MODEL slx_dfd39811daf8
CONFIG AbsTol = auto
CONFIG EnableMultiTasking = off
CONFIG FixedStep = auto
CONFIG InitFcn = Wn = 10;
T = 0.001;
CONFIG MaxStep = auto
CONFIG MinStep = auto
CONFIG RelTol = 1e-3
CONFIG SampleTimeConstraint = Unconstrained
CONFIG SolverName = VariableStepAuto
CONFIG StartTime = 0.0
CONFIG StopTime = 5
BLOCK [CCaller] C Caller
  FunctionName = BPF_Loop
  PortSpecificationStruct = %)30     .    X ,   8    (     @         %    "     (    !     0         %  0 "0    $    _    07)G3F%M90  4&]R=$YA;64 4V-O<&4     26YD97@     5'EP90      4VEZ90      27-';&]B86P   X    X    !@    @    $          4    (     0    4    !         !     %    :6YP=70    .    .     8    (    !          %    "     $    %     0         0    !0   &EN<'5T    #@   #@    &    "     0         !0    @    !    !0...<+936ch>
BLOCK [Constant] Constant2
BLOCK [DataTypeConversion] Data Type Conversion
  RndMeth = Floor
  SaturateOnIntegerOverflow = off
BLOCK [DiscreteTransferFcn] Discrete Transfer Fcn8
  CloseFcn = dspblkCoreblockFVToolHelper(gcbh,'close');
  CopyFcn = dspblkCoreblockFVToolHelper(gcbh,'copy');
  DeleteFcn = dspblkCoreblockFVToolHelper(gcbh,'close');
  Denominator = [(8+8*T*Wn+4*T^2*Wn^2+T^3*Wn^3) (-24-8*T*Wn+4*T^2*Wn^2+3*T^3*Wn^3) (24-8*T*Wn-4*T^2*Wn^2+3*T^3*Wn^3) -8+8*T*Wn-4*T^2*Wn^2+T^3*Wn^3]
  InputPortMap = u0
  LoadFcn = dspblkCoreblockFVToolHelper(gcbh,'load');
  ModelCloseFcn = dspblkCoreblockFVToolHelper(gcbh,'close');
  Numerator = [(T^3*Wn^3) (3*T^3*Wn^3) (3*T^3*Wn^3) T^3*Wn^3]
  PostSaveFcn = dspblkCoreblockFVToolHelper(gcbh,'postsave');
  PreSaveFcn = dspblkCoreblockFVToolHelper(gcbh,'presave');
BLOCK [From] From7
  GotoTag = Signal
BLOCK [From] From9
  GotoTag = Signal
BLOCK [Goto] Goto
  GotoTag = Signal
BLOCK [Scope] Scope5
  ActiveDisplayYMaximum = 1.2063430691042178
  ActiveDisplayYMinimum = -0.13403798128244301
  DataLoggingVariableName = ScopeData5
  Floating = off
  GraphicalSettings = {"Style":{"BackgroundColor":[0.12941176470588237,0.12941176470588237,0.12941176470588237],"AxesColor":[0.07058823529411765,0.07058823529411765,0.07058823529411765],"LabelsColor":[0.8509803921568627,0.8509803921568627,0.8509803921568627],"PreserveColors":false,"Visible":[true,true],"LineStyle":["-","-"],"LineWidth":[1.5,1.5],"BarWidth":[0.9,0.9],"LineColor":["auto","auto"],"LineFaceAlpha":[1,1],"Li...<+2146ch>
  MultipleDisplayCache = [{"MaxYLimMag":1.2063430691042178,"MaxYLimReal":1.2063430691042178,"MinYLimMag":0,"MinYLimReal":-0.13403798128244301,"PlotAsMagnitudePhase":false,"ShowGrid":true,"ShowLegend":true,"Title":"%<SignalLabel>","YLabel":""}]
  NumInputPorts = 2
  ScopeFrameLocation = window
  ShowLegend = on
  WasSavedAsWebScope = on
  WindowPosition = [700.000000,308.000000,560.000000,420.000000,]
BLOCK [Sin] Sine Wave
  Amplitude = 200
  SampleTime = 0
BLOCK [Sin] Sine Wave1
  Amplitude = 8
  Frequency = 50
  SampleTime = 0
BLOCK [Sin] Sine Wave2
  Amplitude = 6
  Frequency = 500
  SampleTime = 0
BLOCK [Sin] Sine Wave3
  Amplitude = 2
  Frequency = 2000
  SampleTime = 0
BLOCK [Sin] Sine Wave4
  Amplitude = 20
  Frequency = 24
  SampleTime = 0
BLOCK [ZeroOrderHold] Zero-Order Hold6
  SampleTime = 0.001
BLOCK [TransferFcn] 一阶低通滤波
  Denominator = [1 Wn]
  Numerator = [Wn]
BLOCK [TransferFcn] 三阶低通滤波
  Denominator = [1 2*Wn 2*Wn^2 Wn^3]
  Numerator = [Wn^3]
BLOCK [TransferFcn] 二阶低通滤波
  Denominator = [1 sqrt(2)*Wn Wn^2]
  Numerator = [Wn^2]
BLOCK [Sum] 原始信号(1rad//s,带多个高频噪声)
  IconShape = rectangular
  Inputs = +++++
BLOCK [Scope] 示波器
  ActiveDisplayYMaximum = 289.66750049431852
  ActiveDisplayYMinimum = -289.523268507868
  DataLoggingVariableName = ScopeData6
  Floating = off
  GraphicalSettings = {"Style":{"BackgroundColor":[0.9019607843137255,0.9019607843137255,0.9019607843137255],"AxesColor":[0.9411764705882353,0.9411764705882353,0.9411764705882353],"LabelsColor":[0.5019607843137255,0.5019607843137255,0.5019607843137255],"PreserveColors":false,"Visible":[true,true,true,true],"LineStyle":["-","-","-","-"],"LineWidth":[1.5,1.5,1.5,1.5],"BarWidth":[0.9,0.9,0.9,0.9],"LineColor":["auto","auto...<+2350ch>
  LayoutDimensionsString = [1,1]
  MultipleDisplayCache = [{"MaxYLimMag":289.66750049431852,"MaxYLimReal":289.66750049431852,"MinYLimMag":0,"MinYLimReal":-289.523268507868,"PlotAsMagnitudePhase":false,"ShowGrid":true,"ShowLegend":true,"Title":"%<SignalLabel>","YLabel":""}]
  NumInputPorts = 4
  ScopeFrameLocation = window
  ShowLegend = on
  WasSavedAsWebScope = on
  WindowPosition = [406.000000,199.000000,933.000000,621.000000,]
LINE C Caller:1 -> Scope5:2
LINE Constant2:1 -> Zero-Order Hold6:1
LINE Data Type Conversion:1 -> C Caller:1
LINE Discrete Transfer Fcn8:1 -> Scope5:1
LINE From7:1 -> 一阶低通滤波:1
LINE From7:1 -> 三阶低通滤波:1
LINE From7:1 -> 二阶低通滤波:1
LINE From9:1 -> 示波器:4
LINE Sine Wave1:1 -> 原始信号(1rad//s,带多个高频噪声):3
LINE Sine Wave2:1 -> 原始信号(1rad//s,带多个高频噪声):4
LINE Sine Wave3:1 -> 原始信号(1rad//s,带多个高频噪声):5
LINE Sine Wave4:1 -> 原始信号(1rad//s,带多个高频噪声):2
LINE Sine Wave:1 -> 原始信号(1rad//s,带多个高频噪声):1
LINE Zero-Order Hold6:1 -> Data Type Conversion:1
LINE Zero-Order Hold6:1 -> Discrete Transfer Fcn8:1
LINE 一阶低通滤波:1 -> 示波器:1
LINE 三阶低通滤波:1 -> 示波器:3
LINE 二阶低通滤波:1 -> 示波器:2
LINE 原始信号(1rad//s,带多个高频噪声):1 -> Goto:1
